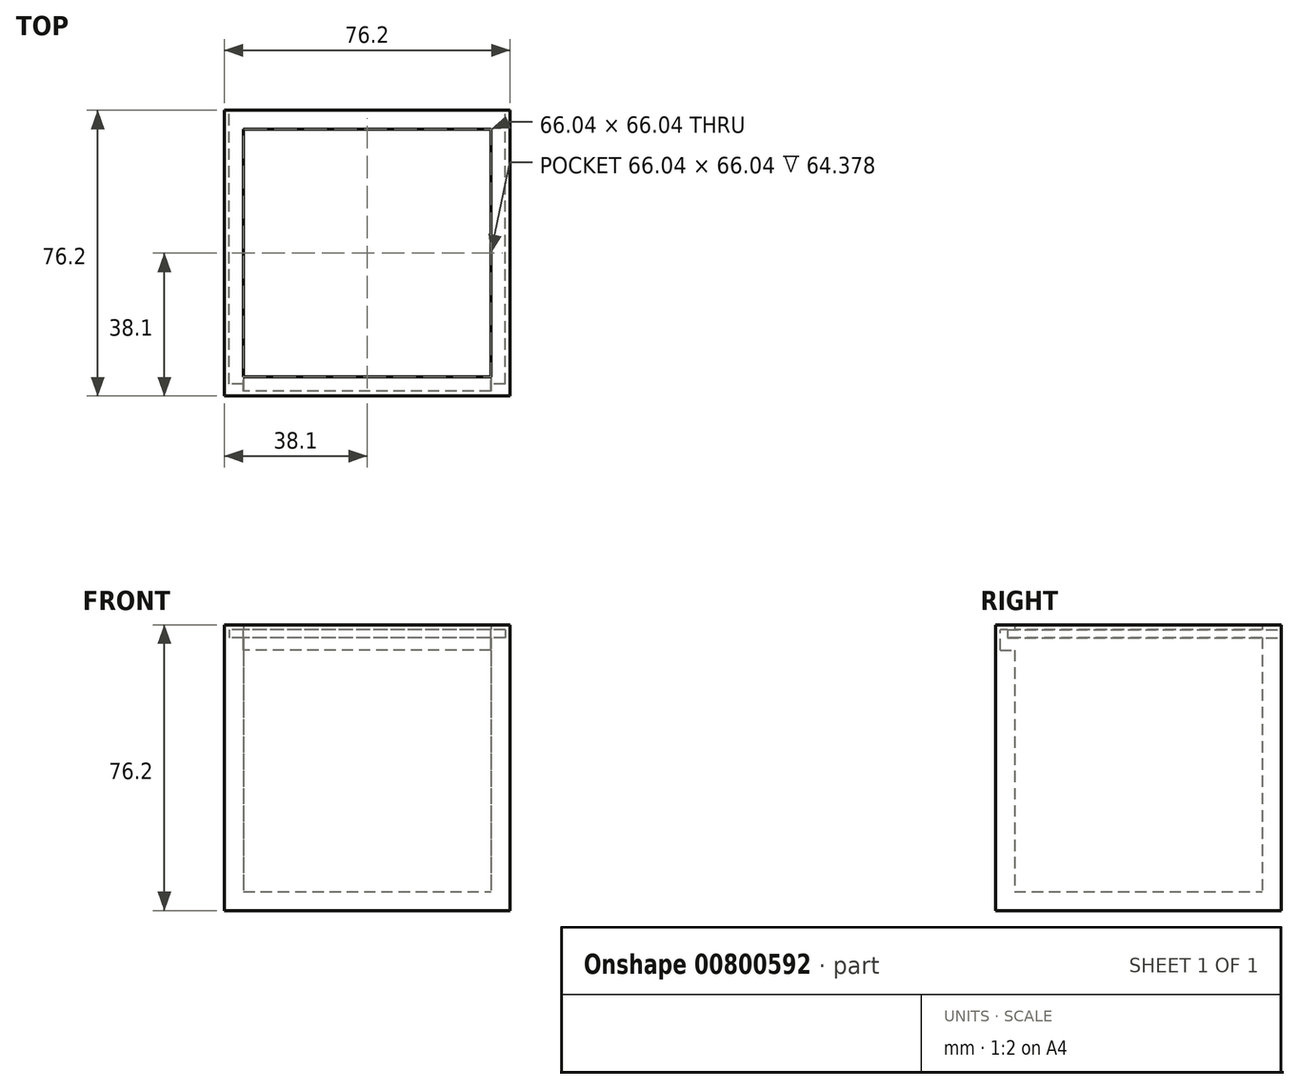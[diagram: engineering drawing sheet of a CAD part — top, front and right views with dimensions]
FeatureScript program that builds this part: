
annotation { "Feature Type Name" : "Feature", "Feature Type Description" : "" }
export const myFeature = defineFeature(function(context is Context, id is Id, definition is map)
    precondition{}
    {
        {
            var Q0;
            Q0=qCreatedBy(makeId("Top.planeOp"),FACE);
            var sketch = newSketch(context, id + "F0", { "sketchPlane" : qUnion([Q0])});
            skLineSegment(sketch, "E0.bottom", {"start": v(-38.1, -38.1) * mm, "end": v(38.1, -38.1) * mm});
            skLineSegment(sketch, "E0.top", {"start": v(-38.1, 38.1) * mm, "end": v(38.1, 38.1) * mm});
            skLineSegment(sketch, "E0.left", {"start": v(-38.1, -38.1) * mm, "end": v(-38.1, 38.1) * mm});
            skLineSegment(sketch, "E0.right", {"start": v(38.1, -38.1) * mm, "end": v(38.1, 38.1) * mm});
            skPoint(sketch, "E0.middle", {"position": v(0, 0) * mm});
            skSolve(sketch);
        }
        {
            var Q0;
            Q0 = qSketchRegion(id + "F0", true);
            extrude(context, id + "F1", {"entities" : qUnion([Q0]), "depth" : 76.2 * mm, "offsetDistance" : 25.4 * mm});
        }
        {
            var Q0;
            Q0=makeQuery(id+"F1.opExtrude","CAP_FACE",FACE,{"disambiguationData":[OSD([sQuery(id+"F0.wireOp",EDGE,"E0.bottom"),sQuery(id+"F0.wireOp",EDGE,"E0.top"),sQuery(id+"F0.wireOp",EDGE,"E0.left"),sQuery(id+"F0.wireOp",EDGE,"E0.right")])],"isStart":false});
            shell(context, id + "F2", {"entities" : qUnion([Q0]), "thickness" : 5.08 * mm});
        }
        {
            var Q0;
            Q0=makeQuery(id+"F1.opExtrude","SWEPT_FACE",FACE,{"disambiguationData":[OSD([sQuery(id+"F0.wireOp",EDGE,"E0.top")])]});
            var sketch = newSketch(context, id + "F3", { "sketchPlane" : qUnion([Q0])});
            skLineSegment(sketch, "E1.bottom", {"start": v(-36.83, 74.93) * mm, "end": v(36.84, 74.93) * mm});
            skLineSegment(sketch, "E1.top", {"start": v(-36.83, 72.77) * mm, "end": v(36.84, 72.77) * mm});
            skLineSegment(sketch, "E1.left", {"start": v(-36.83, 74.93) * mm, "end": v(-36.83, 72.77) * mm});
            skLineSegment(sketch, "E1.right", {"start": v(36.84, 74.93) * mm, "end": v(36.84, 72.77) * mm});
            skSolve(sketch);
        }
        {
            var Q0;
            Q0 = qSketchRegion(id + "F3", true);
            extrude(context, id + "F4", {"entities" : qUnion([Q0]), "operationType" : NewBodyOperationType.REMOVE, "oppositeDirection" : true, "depth" : 74.93 * mm, "offsetDistance" : 25.4 * mm});
        }
        {
            var Q0;
            {var subQ2=sQuery(id+"F0.wireOp",EDGE,"E0.bottom");Q0=makeQuery(id+"F4.boolean.opBoolean","SPLIT",FACE,{"disambiguationData":[TD([makeQuery(id+"F4.opExtrude","SWEPT_FACE",FACE,{"disambiguationData":[OSD([sQuery(id+"F3.wireOp",EDGE,"E1.top")])]})])],"derivedFrom":makeQuery(id+"F2.opShell","OFFSET_FACE",FACE,{"disambiguationData":[OSD([subQ2])]})});}
            var sketch = newSketch(context, id + "F5", { "sketchPlane" : qUnion([Q0])});
            skLineSegment(sketch, "E2.bottom", {"start": v(-33.02, 69.46) * mm, "end": v(33.02, 69.46) * mm});
            skLineSegment(sketch, "E2.top", {"start": v(-33.02, 74.9) * mm, "end": v(33.02, 74.9) * mm});
            skLineSegment(sketch, "E2.left", {"start": v(-33.02, 69.46) * mm, "end": v(-33.02, 74.9) * mm});
            skLineSegment(sketch, "E2.right", {"start": v(33.02, 69.46) * mm, "end": v(33.02, 74.9) * mm});
            skSolve(sketch);
        }
        {
            var Q0;
            Q0 = qSketchRegion(id + "F5", true);
            extrude(context, id + "F6", {"entities" : qUnion([Q0]), "operationType" : NewBodyOperationType.REMOVE, "oppositeDirection" : true, "depth" : 3.8 * mm, "offsetDistance" : 25.4 * mm});
        }
        {
            var Q0;
            Q0=makeQuery(id+"F6.boolean.opBoolean","MERGE",FACE,{"derivedFrom":[makeQuery(id+"F4.boolean.opBoolean","COPY",FACE,{"derivedFrom":makeQuery(id+"F4.opExtrude","CAP_FACE",FACE,{"disambiguationData":[OSD([sQuery(id+"F3.wireOp",EDGE,"E1.bottom"),sQuery(id+"F3.wireOp",EDGE,"E1.top"),sQuery(id+"F3.wireOp",EDGE,"E1.left"),sQuery(id+"F3.wireOp",EDGE,"E1.right")])],"isStart":false})}),makeQuery(id+"F6.opExtrude","CAP_FACE",FACE,{"disambiguationData":[OSD([sQuery(id+"F5.wireOp",EDGE,"E2.bottom"),sQuery(id+"F5.wireOp",EDGE,"E2.top"),sQuery(id+"F5.wireOp",EDGE,"E2.left"),sQuery(id+"F5.wireOp",EDGE,"E2.right")])],"isStart":false})]});
            var sketch = newSketch(context, id + "F7", { "sketchPlane" : qUnion([Q0])});
            skLineSegment(sketch, "E3.bottom", {"start": v(-33.02, 72.77) * mm, "end": v(-36.83, 72.77) * mm});
            skLineSegment(sketch, "E3.top", {"start": v(-33.02, 74.93) * mm, "end": v(-36.83, 74.93) * mm});
            skLineSegment(sketch, "E3.left", {"start": v(-33.02, 72.77) * mm, "end": v(-33.02, 74.93) * mm});
            skLineSegment(sketch, "E3.right", {"start": v(-36.83, 72.77) * mm, "end": v(-36.83, 74.93) * mm});
            skLineSegment(sketch, "E4.bottom", {"start": v(33.02, 72.77) * mm, "end": v(36.84, 72.77) * mm});
            skLineSegment(sketch, "E4.top", {"start": v(33.02, 74.93) * mm, "end": v(36.84, 74.93) * mm});
            skLineSegment(sketch, "E4.left", {"start": v(33.02, 72.77) * mm, "end": v(33.02, 74.93) * mm});
            skLineSegment(sketch, "E4.right", {"start": v(36.84, 72.77) * mm, "end": v(36.84, 74.93) * mm});
            skSolve(sketch);
        }
        {
            var Q0;
            Q0 = qSketchRegion(id + "F7", true);
            extrude(context, id + "F8", {"entities" : qUnion([Q0]), "operationType" : NewBodyOperationType.ADD, "depth" : 1.9 * mm, "offsetDistance" : 25.4 * mm});
        }
    });
